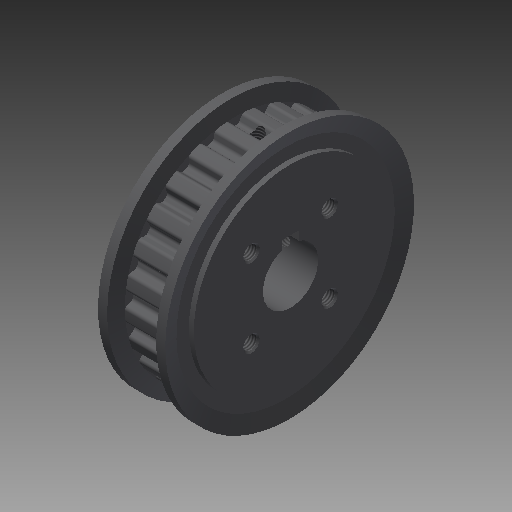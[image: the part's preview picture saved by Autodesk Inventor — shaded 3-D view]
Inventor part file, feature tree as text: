
AUTODESK INVENTOR PART (.ipt)
format: ipt  version: 2017 (Build 210142000, 142)  size: 594,944 bytes
history: native  units: mm
features: other x14, revolve x4, hole x2, extrude x2, thread x2, sketch x2, pattern_linear x1
ambient origin geometry x8: Origin, YZ Plane, XZ Plane, XY Plane, X Axis, Y Axis, Z Axis, Center Point
bodies: Solid1 (feature_tree)
feature tree (27):
  revolve  "Revolution1"  [1 undecoded]
  hole  "Hole1"  [1 undecoded]
  extrude  "Extrusion1"  TaperAngle=360.0deg  [1 undecoded]
  extrude  "Extrusion2"  TaperAngle=360.0deg  [1 undecoded]
  revolve  "Revolution2"  [1 undecoded]
  revolve  "Revolution3"  Angle=360.0deg
  thread  "Thread1"  [1 undecoded]
  revolve  "Revolution4"  [1 undecoded]
  thread  "Thread2"  [1 undecoded]
  hole  "Hole2"  [1 undecoded]
  pattern_linear  "Rectangular Pattern1"  [2 undecoded]
  other  "to_screw1_XY"
  other  "to_screw1_YZ"
  other  "to_screw1_ZX"
  other  "to_screw1_X"
  other  "to_screw1_Y"
  other  "to_screw1_Z"
  other  "to_screw1_Center"
  other  "to_screw2_XY"
  other  "to_screw2_YZ"
  other  "to_screw2_ZX"
  other  "to_screw2_X"
  other  "to_screw2_Y"
  other  "to_screw2_Z"
  other  "to_screw2_Center"
  sketch  "Sketch2"  dims[d0=360.0deg]
  sketch  "Sketch8"  dims[d1=10.0mm d2=6.0mm d3=4.0mm d4=2.0mm d5=90.0deg d6=12.5mm d7=0.0mm d8=7.5mm d9=0.0mm d10=12.5mm d11=0.0mm d12=360.0deg d13=360.0deg d14=13.56mm d15=0.0mm d16=360.0deg d17=14.96mm d18=0.0mm d19=2.459mm d20=6.2705mm d21=3.0mm d22=2.0mm d23=90.0deg d24=8.790148mm d25=120.0deg d26=20.0mm d28=14.142136mm d29=20.0mm d31=14.142136mm d32=0.0mm]
note: 11 required parameter values undecoded (feature->parameter linkage not recoverable at this tier; creation-order binding heuristic only, values carry confidence <= 0.55)